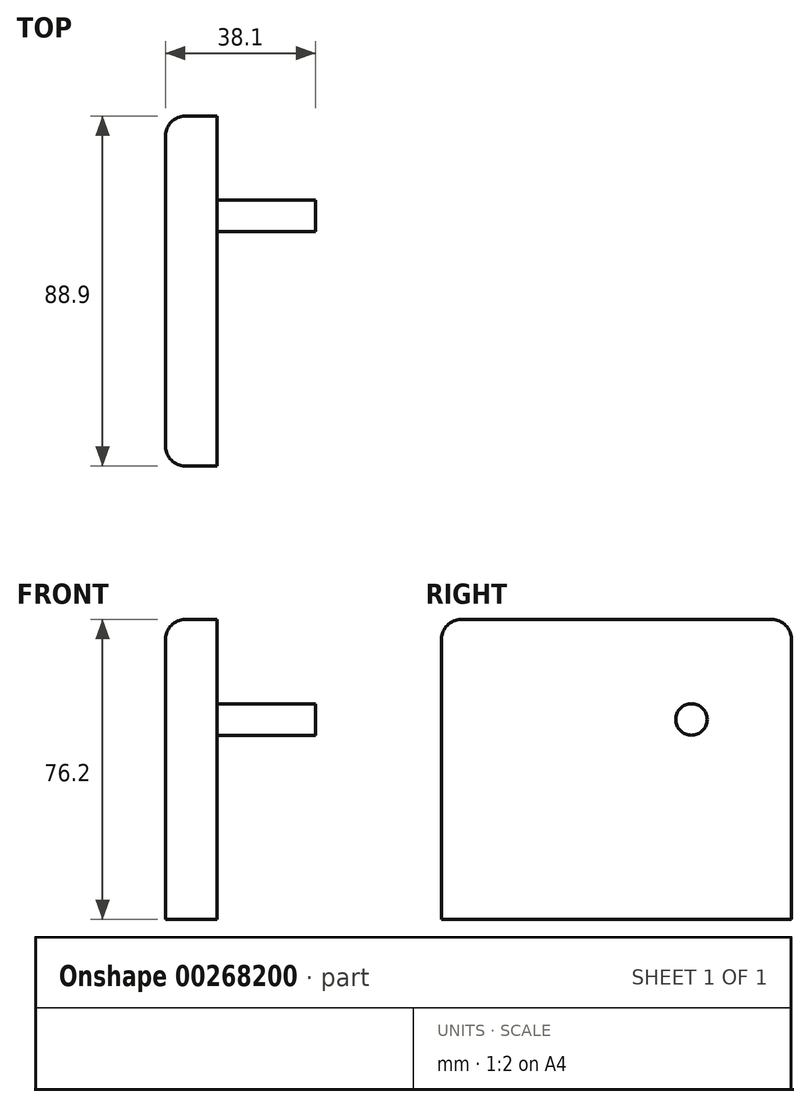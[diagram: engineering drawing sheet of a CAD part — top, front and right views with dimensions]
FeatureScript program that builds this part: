
annotation { "Feature Type Name" : "Feature", "Feature Type Description" : "" }
export const myFeature = defineFeature(function(context is Context, id is Id, definition is map)
    precondition{}
    {
        {
            var Q0;
            Q0=qCreatedBy(makeId("Top.planeOp"),FACE);
            var sketch = newSketch(context, id + "F0", { "sketchPlane" : qUnion([Q0])});
            skLineSegment(sketch, "E0.bottom", {"start": v(-19.05, 44.45) * mm, "end": v(19.05, 44.45) * mm});
            skLineSegment(sketch, "E0.top", {"start": v(-19.05, -44.45) * mm, "end": v(19.05, -44.45) * mm});
            skLineSegment(sketch, "E0.left", {"start": v(-19.05, 44.45) * mm, "end": v(-19.05, -44.45) * mm});
            skLineSegment(sketch, "E0.right", {"start": v(19.05, 44.45) * mm, "end": v(19.05, -44.45) * mm});
            skSolve(sketch);
        }
        {
            var Q0;
            Q0=makeQuery(id+"F0.imprint","IMPRINT",FACE,{"disambiguationData":[TD([[makeQuery(id+"F0.imprint","IMPRINT",EDGE,{"derivedFrom":sQuery(id+"F0.wireOp",EDGE,"E0.bottom")}),-1.0]])]});
            extrude(context, id + "F1", {"entities" : qUnion([Q0]), "depth" : 76.2 * mm});
        }
        {
            var Q0;
            Q0=makeQuery(id+"F1.opExtrude","CAP_FACE",FACE,{"disambiguationData":[OSD([sQuery(id+"F0.wireOp",EDGE,"E0.bottom"),sQuery(id+"F0.wireOp",EDGE,"E0.top"),sQuery(id+"F0.wireOp",EDGE,"E0.left"),sQuery(id+"F0.wireOp",EDGE,"E0.right")])],"isStart":true});
            var sketch = newSketch(context, id + "F2", { "sketchPlane" : qUnion([Q0])});
            skCircle(sketch, "E1", {"center": v(0, 31.75) * mm, "radius": 4 * mm});
            skCircle(sketch, "E2", {"center": v(0, -31.75) * mm, "radius": 4 * mm});
            skSolve(sketch);
        }
        {
            var Q0;
            Q0=makeQuery(id+"F2.imprint","IMPRINT",FACE,{"disambiguationData":[TD([[makeQuery(id+"F2.imprint","IMPRINT",EDGE,{"derivedFrom":sQuery(id+"F2.wireOp",EDGE,"E1")}),1.0]])]});
            var Q1;
            Q1=makeQuery(id+"F2.imprint","IMPRINT",FACE,{"disambiguationData":[TD([[makeQuery(id+"F2.imprint","IMPRINT",EDGE,{"derivedFrom":sQuery(id+"F2.wireOp",EDGE,"E2")}),1.0]])]});
            extrude(context, id + "F3", {"entities" : qUnion([Q0, Q1]), "operationType" : NewBodyOperationType.REMOVE, "oppositeDirection" : true, "depth" : 25 * mm});
        }
        {
            var Q0;
            Q0=makeQuery(id+"F1.opExtrude","SWEPT_FACE",FACE,{"disambiguationData":[OSD([sQuery(id+"F0.wireOp",EDGE,"E0.right")])]});
            var sketch = newSketch(context, id + "F4", { "sketchPlane" : qUnion([Q0])});
            skCircle(sketch, "E3", {"center": v(-19.05, 50.8) * mm, "radius": 4 * mm});
            skCircle(sketch, "E4.MirrorC", {"center": v(19.05, 50.8) * mm, "radius": 4 * mm});
            skSolve(sketch);
        }
        {
            var Q0;
            Q0=makeQuery(id+"F4.imprint","IMPRINT",FACE,{"disambiguationData":[TD([[makeQuery(id+"F4.imprint","IMPRINT",EDGE,{"derivedFrom":sQuery(id+"F4.wireOp",EDGE,"E3")}),1.0]])]});
            var Q1;
            Q1=makeQuery(id+"F4.imprint","IMPRINT",FACE,{"disambiguationData":[TD([[makeQuery(id+"F4.imprint","IMPRINT",EDGE,{"derivedFrom":sQuery(id+"F4.wireOp",EDGE,"E4.MirrorC")}),-1.0]])]});
            extrude(context, id + "F5", {"entities" : qUnion([Q0, Q1]), "operationType" : NewBodyOperationType.REMOVE, "oppositeDirection" : true, "depth" : 25 * mm});
        }
        {
            var Q0;
            Q0=makeQuery(id+"F1.opExtrude","SWEPT_EDGE",EDGE,{"disambiguationData":[OSD([sQuery(id+"F0.wireOp",EDGE,"E0.top"),sQuery(id+"F0.wireOp",EDGE,"E0.left")])]});
            var Q1;
            Q1=makeQuery(id+"F1.opExtrude","SWEPT_EDGE",EDGE,{"disambiguationData":[OSD([sQuery(id+"F0.wireOp",EDGE,"E0.top"),sQuery(id+"F0.wireOp",EDGE,"E0.right")])]});
            var Q2;
            Q2=makeQuery(id+"F1.opExtrude","CAP_EDGE",EDGE,{"disambiguationData":[OSD([sQuery(id+"F0.wireOp",EDGE,"E0.top")])],"isStart":false});
            var Q3;
            Q3=makeQuery(id+"F1.opExtrude","CAP_EDGE",EDGE,{"disambiguationData":[OSD([sQuery(id+"F0.wireOp",EDGE,"E0.left")])],"isStart":false});
            var Q4;
            Q4=makeQuery(id+"F1.opExtrude","CAP_EDGE",EDGE,{"disambiguationData":[OSD([sQuery(id+"F0.wireOp",EDGE,"E0.right")])],"isStart":false});
            var Q5;
            Q5=makeQuery(id+"F1.opExtrude","SWEPT_EDGE",EDGE,{"disambiguationData":[OSD([sQuery(id+"F0.wireOp",EDGE,"E0.bottom"),sQuery(id+"F0.wireOp",EDGE,"E0.right")])]});
            var Q6;
            Q6=makeQuery(id+"F1.opExtrude","CAP_EDGE",EDGE,{"disambiguationData":[OSD([sQuery(id+"F0.wireOp",EDGE,"E0.bottom")])],"isStart":false});
            var Q7;
            Q7=makeQuery(id+"F1.opExtrude","SWEPT_EDGE",EDGE,{"disambiguationData":[OSD([sQuery(id+"F0.wireOp",EDGE,"E0.bottom"),sQuery(id+"F0.wireOp",EDGE,"E0.left")])]});
            fillet(context, id + "F6", {"entities" : qUnion([Q0, Q1, Q2, Q3, Q4, Q5, Q6, Q7]), "radius" : 5 * mm, "tangentPropagation" : true, "allowEdgeOverflow" : false});
        }
    });
